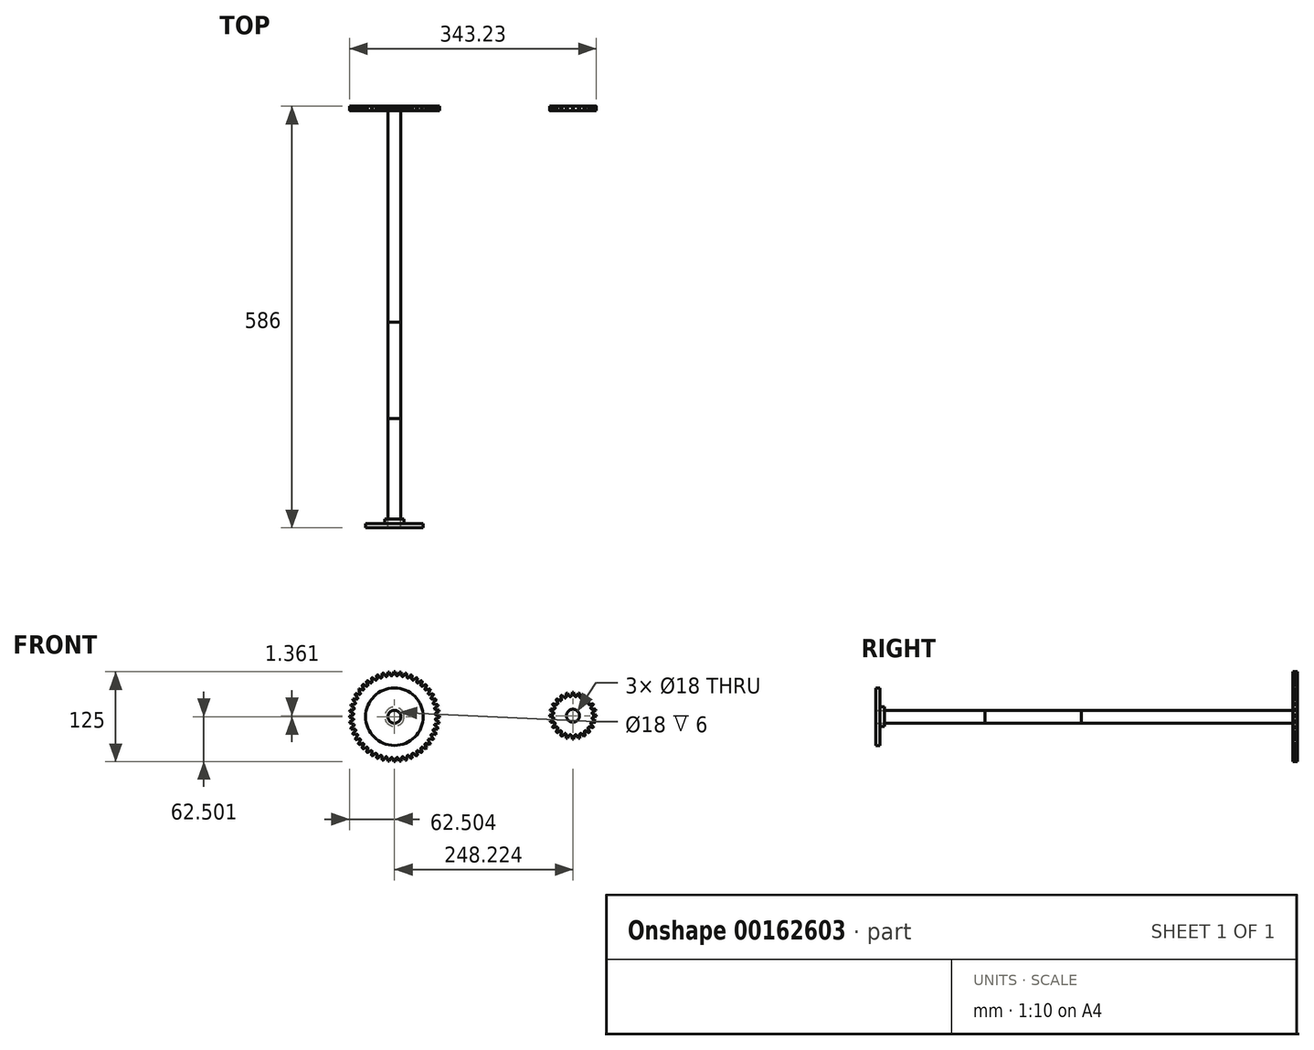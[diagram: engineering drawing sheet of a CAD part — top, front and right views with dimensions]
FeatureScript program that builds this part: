
annotation { "Feature Type Name" : "Feature", "Feature Type Description" : "" }
export const myFeature = defineFeature(function(context is Context, id is Id, definition is map)
    precondition{}
    {
        {
            var Q0;
            Q0=qCreatedBy(makeId("Front.planeOp"),FACE);
            var sketch = newSketch(context, id + "F0", { "sketchPlane" : qUnion([Q0])});
            skArc(sketch, "E0", {"start": v(-143.94, 36.02) * mm, "mid": v(-144.9, 36.03) * mm, "end": v(-145.87, 36.02) * mm});
            skArc(sketch, "E1", {"start": v(-147.5, 30.95) * mm, "mid": v(-147.84, 30.48) * mm, "end": v(-148.39, 30.3) * mm});
            skCircle(sketch, "E2", {"center": v(-144.9, -26.47) * mm, "radius": 56.87 * mm});
            skCircle(sketch, "E3", {"center": v(-144.9, -26.47) * mm, "radius": 9 * mm});
            skLineSegment(sketch, "E4", {"start": v(-145.87, 36.02) * mm, "end": v(-147.5, 30.95) * mm});
            skLineSegment(sketch, "E5", {"start": v(-144.9, 36.03) * mm, "end": v(-144.9, 33.44) * mm, "construction": true});
            skLineSegment(sketch, "E6.MirrorCS", {"start": v(-143.94, 36.02) * mm, "end": v(-142.31, 30.95) * mm});
            skArc(sketch, "E7.MirrorCS", {"start": v(-142.31, 30.95) * mm, "mid": v(-141.97, 30.48) * mm, "end": v(-141.43, 30.3) * mm});
            skSolve(sketch);
        }
        {
            var Q0;
            Q0=qCreatedBy(makeId("Right.planeOp"),FACE);
            var Q1;
            Q1=sQuery(id+"F0.wireOp",VERTEX,"E0.center");
            cPlane(context, id + "F1", {"entities" : qUnion([Q0, Q1]), "cplaneType" : CPlaneType.PLANE_POINT, "offset" : 25 * mm, "width" : 150 * mm, "height" : 150 * mm});
        }
        {
            var Q0;
            Q0=qCreatedBy(id+"F1.planeOp",FACE);
            var sketch = newSketch(context, id + "F2", { "sketchPlane" : qUnion([Q0])});
            skLineSegment(sketch, "E8", {"start": v(0, -26.47) * mm, "end": v(-77.1, -26.47) * mm, "construction": true});
            skSolve(sketch);
        }
        {
            var Q0;
            Q0=makeQuery(id+"F0.imprint","IMPRINT",FACE,{"disambiguationData":[TD([[makeQuery(id+"F0.imprint","IMPRINT",EDGE,{"derivedFrom":sQuery(id+"F0.wireOp",EDGE,"E3")}),-1.0]])]});
            extrude(context, id + "F3", {"entities" : qUnion([Q0]), "depth" : 6 * mm});
        }
        {
            var Q0;
            Q0=makeQuery(id+"F0.imprint","IMPRINT",FACE,{"disambiguationData":[TD([[makeQuery(id+"F0.imprint","IMPRINT",EDGE,{"derivedFrom":sQuery(id+"F0.wireOp",EDGE,"E0")}),1.0]])]});
            extrude(context, id + "F4", {"entities" : qUnion([Q0]), "depth" : 6 * mm});
        }
        {
            var Q0;
            Q0=makeQuery(id+"F4.opExtrude","SWEPT_BODY",BODY,{"disambiguationData":[OSD([sQuery(id+"F0.wireOp",EDGE,"d17c9a9a-b1a7-4931-965a-7dbf0318c6ea"),sQuery(id+"F0.wireOp",EDGE,"aae1c5f8-cb92-46c1-bb2a-699cb83fedbd"),sQuery(id+"F0.wireOp",EDGE,"11cfcc7c-25a6-47fb-ba93-4a799e7af8d9"),sQuery(id+"F0.wireOp",EDGE,"E0"),sQuery(id+"F0.wireOp",EDGE,"cdab2608-0d30-43e0-861b-7dcc17d285da"),sQuery(id+"F0.wireOp",EDGE,"82bfc3b3-f438-4078-b01b-72c0e55f7540"),sQuery(id+"F0.wireOp",EDGE,"E1"),sQuery(id+"F0.wireOp",EDGE,"2f7f638c-8028-41ff-8f82-c0bb453953b0")])]});
            var Q1;
            Q1=sQuery(id+"F2.wireOp",EDGE,"E8");
            circularPattern(context, id + "F5", {"operationType" : NewBodyOperationType.ADD, "entities" : qUnion([Q0]), "axis" : qUnion([Q1]), "angle" : 360 * degree, "instanceCount" : 48, "equalSpace" : true});
        }
        {
            var Q0;
            Q0=qCreatedBy(makeId("Front.planeOp"),FACE);
            var sketch = newSketch(context, id + "F6", { "sketchPlane" : qUnion([Q0])});
            skArc(sketch, "E9", {"start": v(104.21, 7.38) * mm, "mid": v(103.32, 7.4) * mm, "end": v(102.42, 7.38) * mm});
            skArc(sketch, "E10", {"start": v(101.06, 2.28) * mm, "mid": v(100.76, 1.81) * mm, "end": v(100.26, 1.59) * mm});
            skCircle(sketch, "E11", {"center": v(103.32, -25.1) * mm, "radius": 26.87 * mm});
            skCircle(sketch, "E12", {"center": v(103.32, -25.1) * mm, "radius": 9 * mm});
            skLineSegment(sketch, "E13", {"start": v(102.42, 7.38) * mm, "end": v(101.06, 2.28) * mm});
            skLineSegment(sketch, "E14", {"start": v(103.32, 7.4) * mm, "end": v(103.32, 5.1) * mm, "construction": true});
            skLineSegment(sketch, "E15.MirrorCS", {"start": v(104.21, 7.38) * mm, "end": v(105.58, 2.28) * mm});
            skArc(sketch, "E16.MirrorCS", {"start": v(105.58, 2.28) * mm, "mid": v(105.87, 1.81) * mm, "end": v(106.38, 1.59) * mm});
            skSolve(sketch);
        }
        {
            var Q0;
            Q0=qCreatedBy(makeId("Right.planeOp"),FACE);
            var Q1;
            Q1=sQuery(id+"F6.wireOp",VERTEX,"E9.center");
            cPlane(context, id + "F7", {"entities" : qUnion([Q0, Q1]), "cplaneType" : CPlaneType.PLANE_POINT, "offset" : 25 * mm, "width" : 150 * mm, "height" : 150 * mm});
        }
        {
            var Q0;
            Q0=qCreatedBy(id+"F7.planeOp",FACE);
            var sketch = newSketch(context, id + "F8", { "sketchPlane" : qUnion([Q0])});
            skLineSegment(sketch, "E17", {"start": v(0, -25.1) * mm, "end": v(-81.44, -25.1) * mm, "construction": true});
            skSolve(sketch);
        }
        {
            var Q0;
            Q0=makeQuery(id+"F6.imprint","IMPRINT",FACE,{"disambiguationData":[TD([[makeQuery(id+"F6.imprint","IMPRINT",EDGE,{"derivedFrom":sQuery(id+"F6.wireOp",EDGE,"E12")}),-1.0]])]});
            extrude(context, id + "F9", {"entities" : qUnion([Q0]), "depth" : 6 * mm});
        }
        {
            var Q0;
            Q0=makeQuery(id+"F6.imprint","IMPRINT",FACE,{"disambiguationData":[TD([[makeQuery(id+"F6.imprint","IMPRINT",EDGE,{"derivedFrom":sQuery(id+"F6.wireOp",EDGE,"E9")}),1.0]])]});
            extrude(context, id + "F10", {"entities" : qUnion([Q0]), "depth" : 6 * mm});
        }
        {
            var Q0;
            Q0=makeQuery(id+"F10.opExtrude","SWEPT_BODY",BODY,{"disambiguationData":[OSD([sQuery(id+"F6.wireOp",EDGE,"2baffc8f-243c-429a-8163-9cec3509ba41"),sQuery(id+"F6.wireOp",EDGE,"eb38847a-13aa-4753-a2db-66340823ec47"),sQuery(id+"F6.wireOp",EDGE,"25fbddf5-5604-4575-b976-a73180309192"),sQuery(id+"F6.wireOp",EDGE,"ea08bd5f-8ba8-4089-9439-fad37d6e2f33"),sQuery(id+"F6.wireOp",EDGE,"E9"),sQuery(id+"F6.wireOp",EDGE,"82739327-4280-468d-a813-0a7ebf70fc2d"),sQuery(id+"F6.wireOp",EDGE,"808db2cd-8ebf-4573-a6f4-9c469a4fcd93"),sQuery(id+"F6.wireOp",EDGE,"01fc9465-3709-414d-88a4-4cf867339ef8"),sQuery(id+"F6.wireOp",EDGE,"E10"),sQuery(id+"F6.wireOp",EDGE,"E11")])]});
            var Q1;
            Q1=sQuery(id+"F8.wireOp",EDGE,"E17");
            circularPattern(context, id + "F11", {"operationType" : NewBodyOperationType.ADD, "entities" : qUnion([Q0]), "axis" : qUnion([Q1]), "angle" : 360 * degree, "instanceCount" : 24, "equalSpace" : true});
        }
        {
            var Q0;
            Q0=makeQuery(id+"F0.imprint","IMPRINT",FACE,{"disambiguationData":[TD([[makeQuery(id+"F0.imprint","IMPRINT",EDGE,{"derivedFrom":sQuery(id+"F0.wireOp",EDGE,"E3")}),1.0]])]});
            extrude(context, id + "F12", {"entities" : qUnion([Q0]), "depth" : 300 * mm});
        }
        {
            var Q0;
            Q0=makeQuery(id+"F12.opExtrude","CAP_FACE",FACE,{"disambiguationData":[OSD([sQuery(id+"F0.wireOp",EDGE,"E3")])],"isStart":false});
            extrude(context, id + "F13", {"entities" : qUnion([Q0]), "depth" : 134 * mm});
        }
        {
            var Q0;
            Q0=makeQuery(id+"F13.opExtrude","CAP_FACE",FACE,{"disambiguationData":[OSD([sQuery(id+"F0.wireOp",EDGE,"E3")])],"isStart":false});
            extrude(context, id + "F14", {"entities" : qUnion([Q0]), "depth" : 140 * mm});
        }
        {
            var Q0;
            Q0=makeQuery(id+"F14.opExtrude","CAP_FACE",FACE,{"disambiguationData":[OSD([sQuery(id+"F0.wireOp",EDGE,"E3")])],"isStart":false});
            var sketch = newSketch(context, id + "F15", { "sketchPlane" : qUnion([Q0])});
            skCircle(sketch, "E18", {"center": v(-144.9, -26.47) * mm, "radius": 9 * mm});
            skCircle(sketch, "E19", {"center": v(-144.9, -26.47) * mm, "radius": 13.5 * mm});
            skSolve(sketch);
        }
        {
            var Q0;
            Q0=qSketchRegion(id+"F15",true);
            extrude(context, id + "F16", {"entities" : qUnion([Q0]), "depth" : 6 * mm});
        }
        {
            var Q0;
            Q0=makeQuery(id+"F16.opExtrude","CAP_FACE",FACE,{"disambiguationData":[OSD([sQuery(id+"F15.wireOp",EDGE,"E18"),sQuery(id+"F15.wireOp",EDGE,"E19")])],"isStart":false});
            var sketch = newSketch(context, id + "F17", { "sketchPlane" : qUnion([Q0])});
            skCircle(sketch, "E20", {"center": v(-144.9, -26.47) * mm, "radius": 40 * mm});
            skCircle(sketch, "E21", {"center": v(-144.9, -26.47) * mm, "radius": 9 * mm});
            skSolve(sketch);
        }
        {
            var Q0;
            Q0=qSketchRegion(id+"F17",true);
            extrude(context, id + "F18", {"entities" : qUnion([Q0]), "depth" : 6 * mm});
        }
    });
